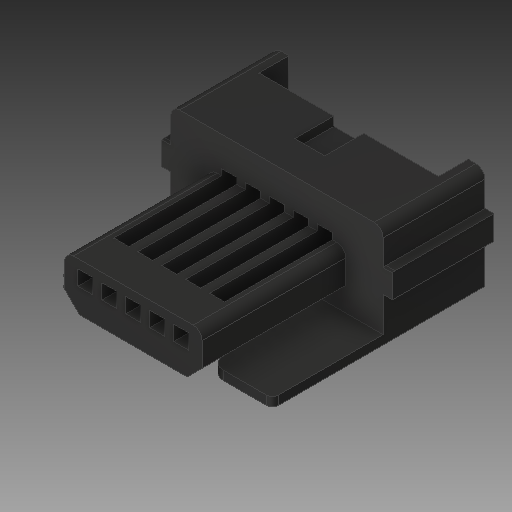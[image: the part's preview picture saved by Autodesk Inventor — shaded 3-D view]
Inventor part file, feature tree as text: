
AUTODESK INVENTOR PART (.ipt)
format: ipt  version: 2019.4 (Build 234330000, 330)  size: 201,728 bytes
history: native  units: mm
features: fillet x1
ambient origin geometry x8: Origin, YZ Plane, XZ Plane, XY Plane, X Axis, Y Axis, Z Axis, Center Point
bodies: Solid1 (feature_tree)
feature tree (1):
  fillet  "Fillet3"  [1 undecoded]
note: 1 required parameter value undecoded (feature->parameter linkage not recoverable at this tier; creation-order binding heuristic only, values carry confidence <= 0.55)
